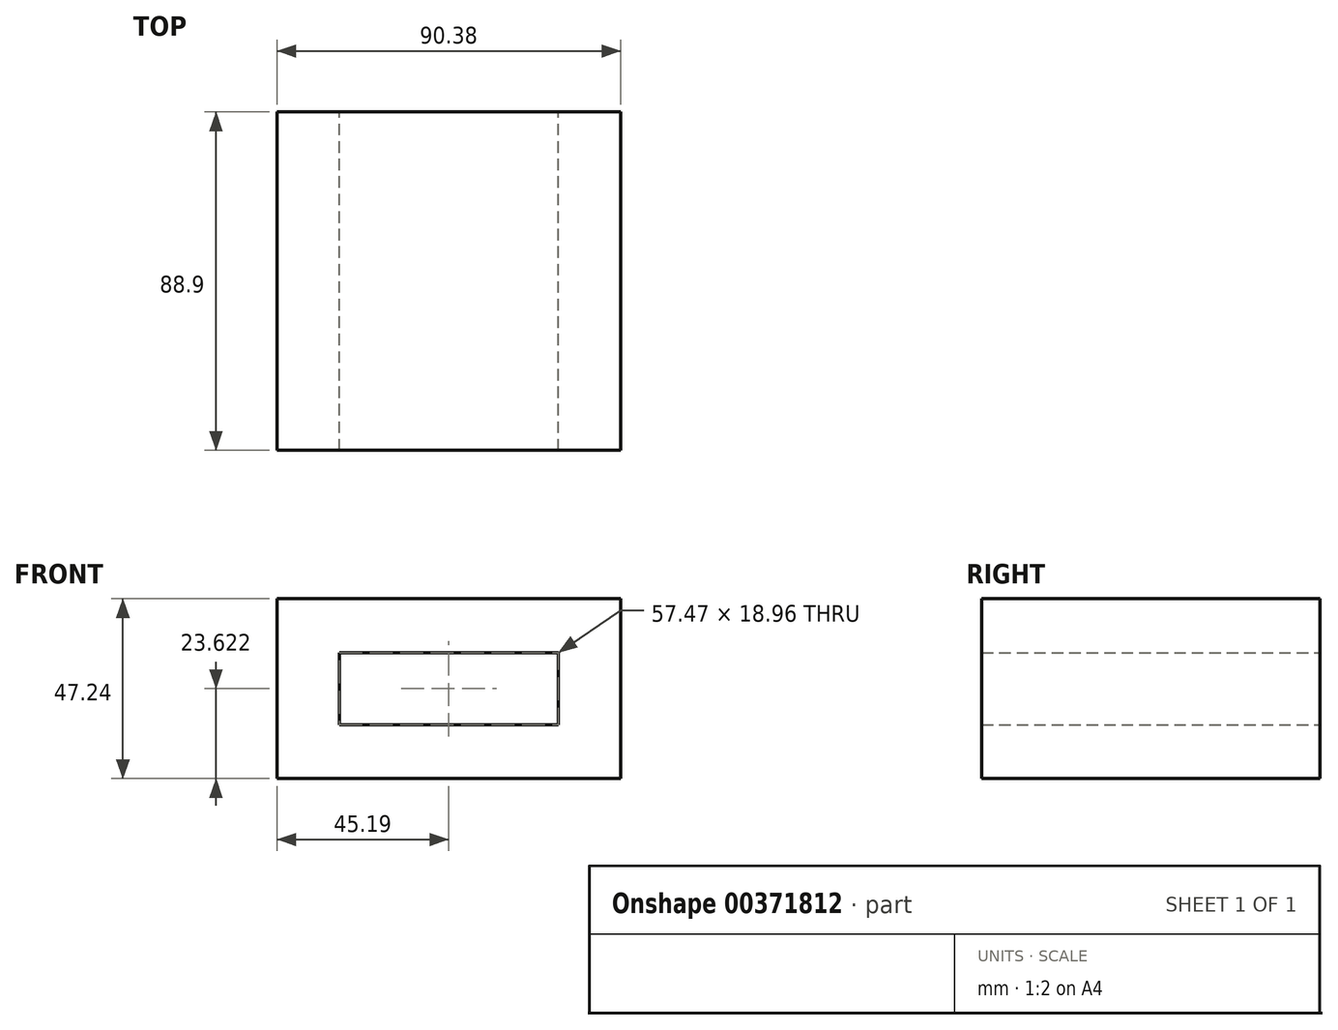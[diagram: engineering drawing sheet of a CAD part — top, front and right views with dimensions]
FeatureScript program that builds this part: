
annotation { "Feature Type Name" : "Feature", "Feature Type Description" : "" }
export const myFeature = defineFeature(function(context is Context, id is Id, definition is map)
    precondition{}
    {
        {
            var Q0;
            Q0=qCreatedBy(makeId("Front.planeOp"),FACE);
            var sketch = newSketch(context, id + "F0", { "sketchPlane" : qUnion([Q0])});
            skLineSegment(sketch, "E0.bottom", {"start": v(23.21, -17.4) * mm, "end": v(-67.17, -17.4) * mm});
            skLineSegment(sketch, "E0.top", {"start": v(23.21, 29.85) * mm, "end": v(-67.17, 29.85) * mm});
            skLineSegment(sketch, "E0.left", {"start": v(23.21, -17.4) * mm, "end": v(23.21, 29.85) * mm});
            skLineSegment(sketch, "E0.right", {"start": v(-67.17, -17.4) * mm, "end": v(-67.17, 29.85) * mm});
            skPoint(sketch, "E0.middle", {"position": v(-21.98, 6.23) * mm});
            skLineSegment(sketch, "E1.bottom", {"start": v(6.75, -3.25) * mm, "end": v(-50.72, -3.25) * mm});
            skLineSegment(sketch, "E1.top", {"start": v(6.75, 15.71) * mm, "end": v(-50.72, 15.71) * mm});
            skLineSegment(sketch, "E1.left", {"start": v(6.75, -3.25) * mm, "end": v(6.75, 15.71) * mm});
            skLineSegment(sketch, "E1.right", {"start": v(-50.72, -3.25) * mm, "end": v(-50.72, 15.71) * mm});
            skSolve(sketch);
        }
        {
            var Q0;
            Q0=makeQuery(id+"F0.imprint","IMPRINT",FACE,{"disambiguationData":[TD([[makeQuery(id+"F0.imprint","IMPRINT",EDGE,{"derivedFrom":sQuery(id+"F0.wireOp",EDGE,"E0.bottom")}),-1.0]])]});
            extrude(context, id + "F1", {"entities" : qUnion([Q0]), "endBound" : BoundingType.SYMMETRIC, "depth" : 50.8 * mm});
        }
        {
            var Q0;
            Q0=makeQuery(id+"F1.opExtrude","CAP_FACE",FACE,{"disambiguationData":[OSD([sQuery(id+"F0.wireOp",EDGE,"E0.bottom"),sQuery(id+"F0.wireOp",EDGE,"E0.top"),sQuery(id+"F0.wireOp",EDGE,"E0.left"),sQuery(id+"F0.wireOp",EDGE,"E0.right"),sQuery(id+"F0.wireOp",EDGE,"E1.bottom"),sQuery(id+"F0.wireOp",EDGE,"E1.top"),sQuery(id+"F0.wireOp",EDGE,"E1.left"),sQuery(id+"F0.wireOp",EDGE,"E1.right")])],"isStart":false});
            extrude(context, id + "F2", {"entities" : qUnion([Q0]), "operationType" : NewBodyOperationType.ADD, "depth" : 25.4 * mm});
        }
        {
            var Q0;
            Q0=makeQuery(id+"F2.opExtrude","CAP_FACE",FACE,{"disambiguationData":[OSD([sQuery(id+"F0.wireOp",EDGE,"E0.bottom"),sQuery(id+"F0.wireOp",EDGE,"E0.top"),sQuery(id+"F0.wireOp",EDGE,"E0.left"),sQuery(id+"F0.wireOp",EDGE,"E0.right"),sQuery(id+"F0.wireOp",EDGE,"E1.bottom"),sQuery(id+"F0.wireOp",EDGE,"E1.top"),sQuery(id+"F0.wireOp",EDGE,"E1.left"),sQuery(id+"F0.wireOp",EDGE,"E1.right")])],"isStart":false});
            extrude(context, id + "F3", {"entities" : qUnion([Q0]), "operationType" : NewBodyOperationType.ADD, "depth" : 12.7 * mm});
        }
    });
